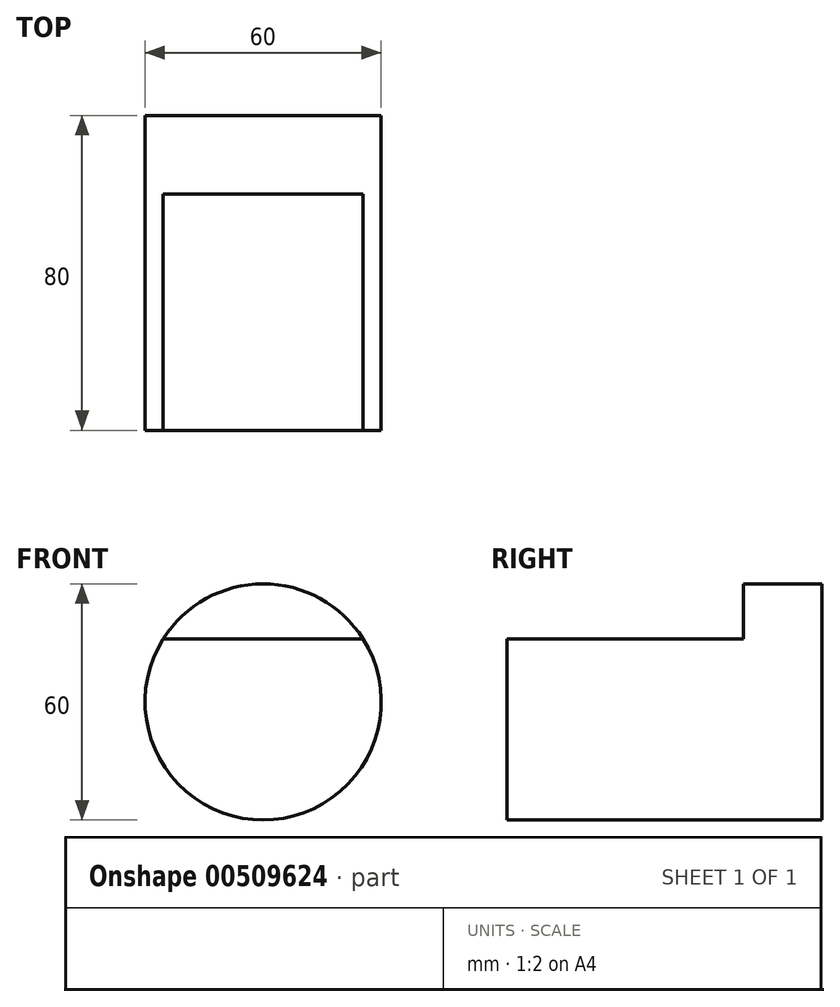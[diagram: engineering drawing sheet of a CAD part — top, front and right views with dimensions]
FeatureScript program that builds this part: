
annotation { "Feature Type Name" : "Feature", "Feature Type Description" : "" }
export const myFeature = defineFeature(function(context is Context, id is Id, definition is map)
    precondition{}
    {
        {
            var Q0;
            Q0=qCreatedBy(makeId("Front.planeOp"),FACE);
            var sketch = newSketch(context, id + "F0", { "sketchPlane" : qUnion([Q0])});
            skCircle(sketch, "E0", {"center": v(0, 0) * mm, "radius": 30 * mm});
            skSolve(sketch);
        }
        {
            var Q0;
            Q0=makeQuery(id+"F0.imprint","IMPRINT",FACE,{"disambiguationData":[TD([[makeQuery(id+"F0.imprint","IMPRINT",EDGE,{"derivedFrom":sQuery(id+"F0.wireOp",EDGE,"E0")}),1.0]])]});
            extrude(context, id + "F1", {"entities" : qUnion([Q0]), "endBound" : BoundingType.SYMMETRIC, "depth" : 80 * mm});
        }
        {
            var Q0;
            Q0=makeQuery(id+"F1.opExtrude","CAP_FACE",FACE,{"disambiguationData":[OSD([sQuery(id+"F0.wireOp",EDGE,"E0")])],"isStart":false});
            var sketch = newSketch(context, id + "F2", { "sketchPlane" : qUnion([Q0])});
            skLineSegment(sketch, "E1", {"start": v(25.38, 16) * mm, "end": v(-25.38, 16) * mm});
            skArc(sketch, "E2.0", {"start": v(25.38, 16) * mm, "mid": v(0, 30) * mm, "end": v(-25.38, 16) * mm});
            skSolve(sketch);
        }
        {
            var Q0;
            Q0=makeQuery(id+"F2.imprint","IMPRINT",FACE,{"disambiguationData":[TD([[makeQuery(id+"F2.imprint","IMPRINT",EDGE,{"derivedFrom":sQuery(id+"F2.wireOp",EDGE,"E1")}),-1.0]])]});
            extrude(context, id + "F3", {"entities" : qUnion([Q0]), "operationType" : NewBodyOperationType.REMOVE, "oppositeDirection" : true, "depth" : 60 * mm});
        }
    });
